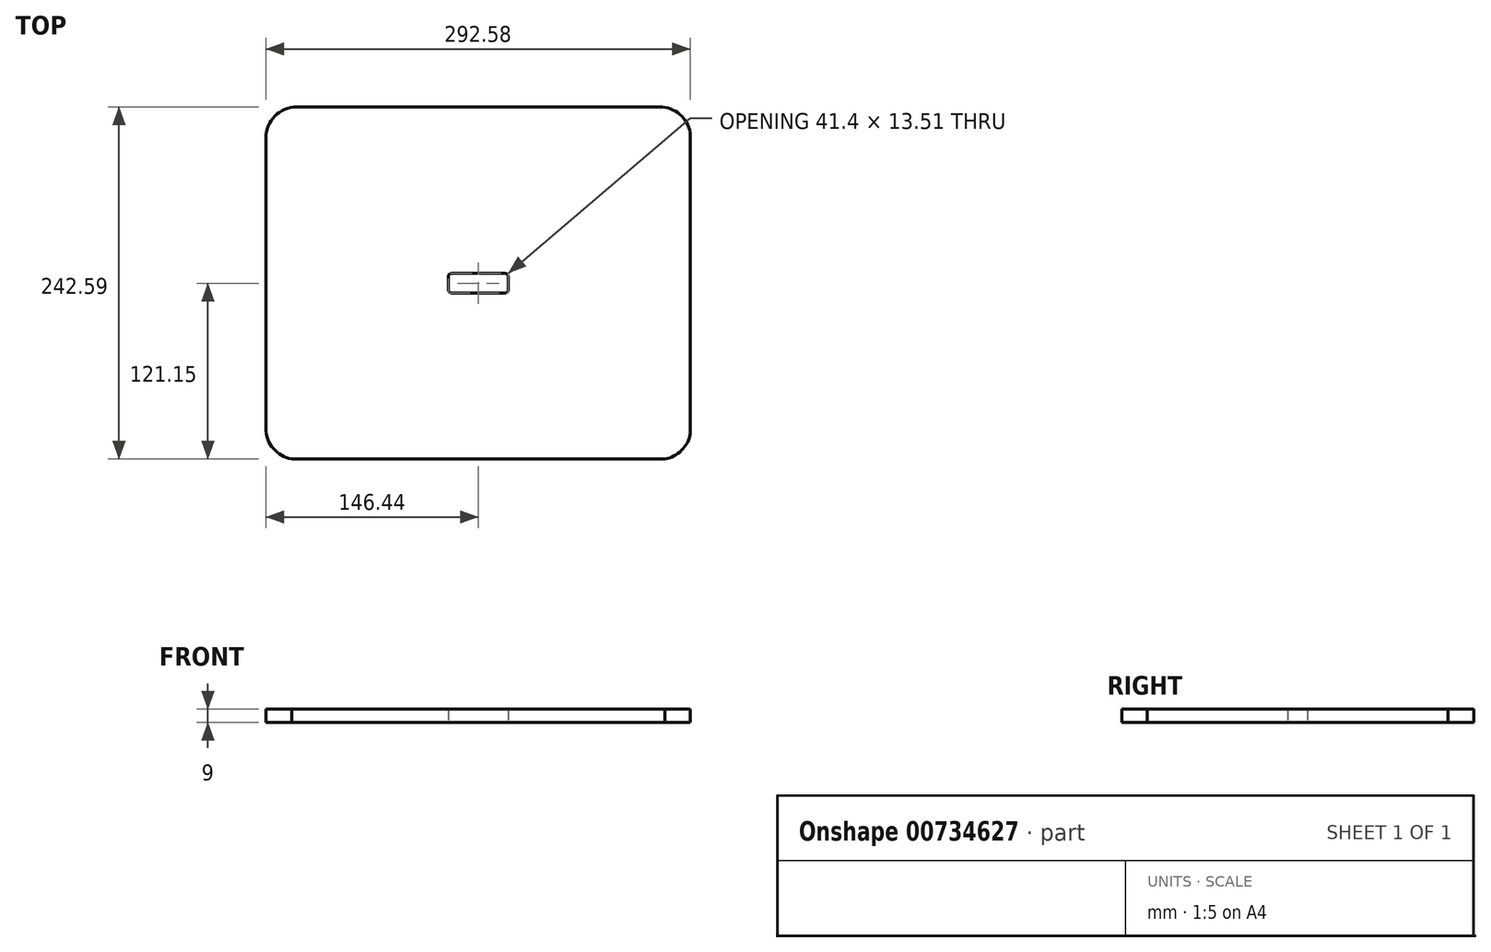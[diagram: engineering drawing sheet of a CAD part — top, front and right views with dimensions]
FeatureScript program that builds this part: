
annotation { "Feature Type Name" : "Feature", "Feature Type Description" : "" }
export const myFeature = defineFeature(function(context is Context, id is Id, definition is map)
    precondition{}
    {
        {
            var Q0;
            Q0=qCreatedBy(makeId("Top.planeOp"),FACE);
            var sketch = newSketch(context, id + "F0", { "sketchPlane" : qUnion([Q0])});
            skLineSegment(sketch, "E0.bottom", {"start": v(-125, 121.44) * mm, "end": v(125, 121.44) * mm});
            skLineSegment(sketch, "E0.top", {"start": v(-128.48, -121.15) * mm, "end": v(128.48, -121.15) * mm});
            skLineSegment(sketch, "E0.left", {"start": v(-146.44, 100) * mm, "end": v(-146.44, -100) * mm});
            skLineSegment(sketch, "E0.right", {"start": v(146.14, 103.54) * mm, "end": v(146.14, -103.54) * mm});
            skPoint(sketch, "E1.visualSharp", {"position": v(-146.44, 121.44) * mm});
            skArc(sketch, "E1.filletArc", {"start": v(-125, 121.44) * mm, "mid": v(-140.16, 115.16) * mm, "end": v(-146.44, 100) * mm});
            skArc(sketch, "E2.MirrorCS", {"start": v(125, 121.44) * mm, "mid": v(140.16, 115.16) * mm, "end": v(146.44, 100) * mm});
            skArc(sketch, "E3.MirrorCS", {"start": v(-125, -121.44) * mm, "mid": v(-140.16, -115.16) * mm, "end": v(-146.44, -100) * mm});
            skArc(sketch, "E4.MirrorCS", {"start": v(125, -121.44) * mm, "mid": v(140.16, -115.16) * mm, "end": v(146.44, -100) * mm});
            skLineSegment(sketch, "E5.right", {"start": v(-20.7, 0) * mm, "end": v(-20.7, 4.4) * mm});
            skPoint(sketch, "E6.visualSharp", {"position": v(-20.7, 6.75) * mm});
            skArc(sketch, "E6.filletArc", {"start": v(-18.35, 6.75) * mm, "mid": v(-20.01, 6.07) * mm, "end": v(-20.7, 4.4) * mm});
            skArc(sketch, "E7.MirrorCS", {"start": v(18.35, 6.75) * mm, "mid": v(20.01, 6.07) * mm, "end": v(20.7, 4.4) * mm});
            skLineSegment(sketch, "E8.MirrorCS", {"start": v(20.7, 0) * mm, "end": v(20.7, 4.4) * mm});
            skPoint(sketch, "E9.MirrorP", {"position": v(20.7, 6.75) * mm});
            skArc(sketch, "E10.MirrorCS", {"start": v(-18.35, -6.75) * mm, "mid": v(-20.01, -6.07) * mm, "end": v(-20.7, -4.4) * mm});
            skArc(sketch, "E11.MirrorCS", {"start": v(18.35, -6.75) * mm, "mid": v(20.01, -6.07) * mm, "end": v(20.7, -4.4) * mm});
            skLineSegment(sketch, "E12.MirrorCS", {"start": v(20.7, 0) * mm, "end": v(20.7, -4.4) * mm});
            skLineSegment(sketch, "E13.MirrorCS", {"start": v(-20.7, 0) * mm, "end": v(-20.7, -4.4) * mm});
            skPoint(sketch, "E14.MirrorP", {"position": v(20.7, -6.75) * mm});
            skPoint(sketch, "E15.MirrorP", {"position": v(-20.7, -6.75) * mm});
            skLineSegment(sketch, "E16", {"start": v(-18.35, 6.75) * mm, "end": v(18.35, 6.75) * mm});
            skLineSegment(sketch, "E17", {"start": v(-18.35, -6.75) * mm, "end": v(18.35, -6.75) * mm});
            skSolve(sketch);
        }
        {
            var Q0;
            {var subQ6=sQuery(id+"F0.wireOp",EDGE,"E0.bottom");Q0=makeQuery(id+"F0.imprint","IMPRINT",FACE,{"disambiguationData":[TD([[makeQuery(id+"F0.imprint","IMPRINT",EDGE,{"derivedFrom":subQ6}),-1.0]])]});}
            extrude(context, id + "F1", {"entities" : qUnion([Q0]), "depth" : 9 * mm, "offsetDistance" : 25.4 * mm});
        }
    });
